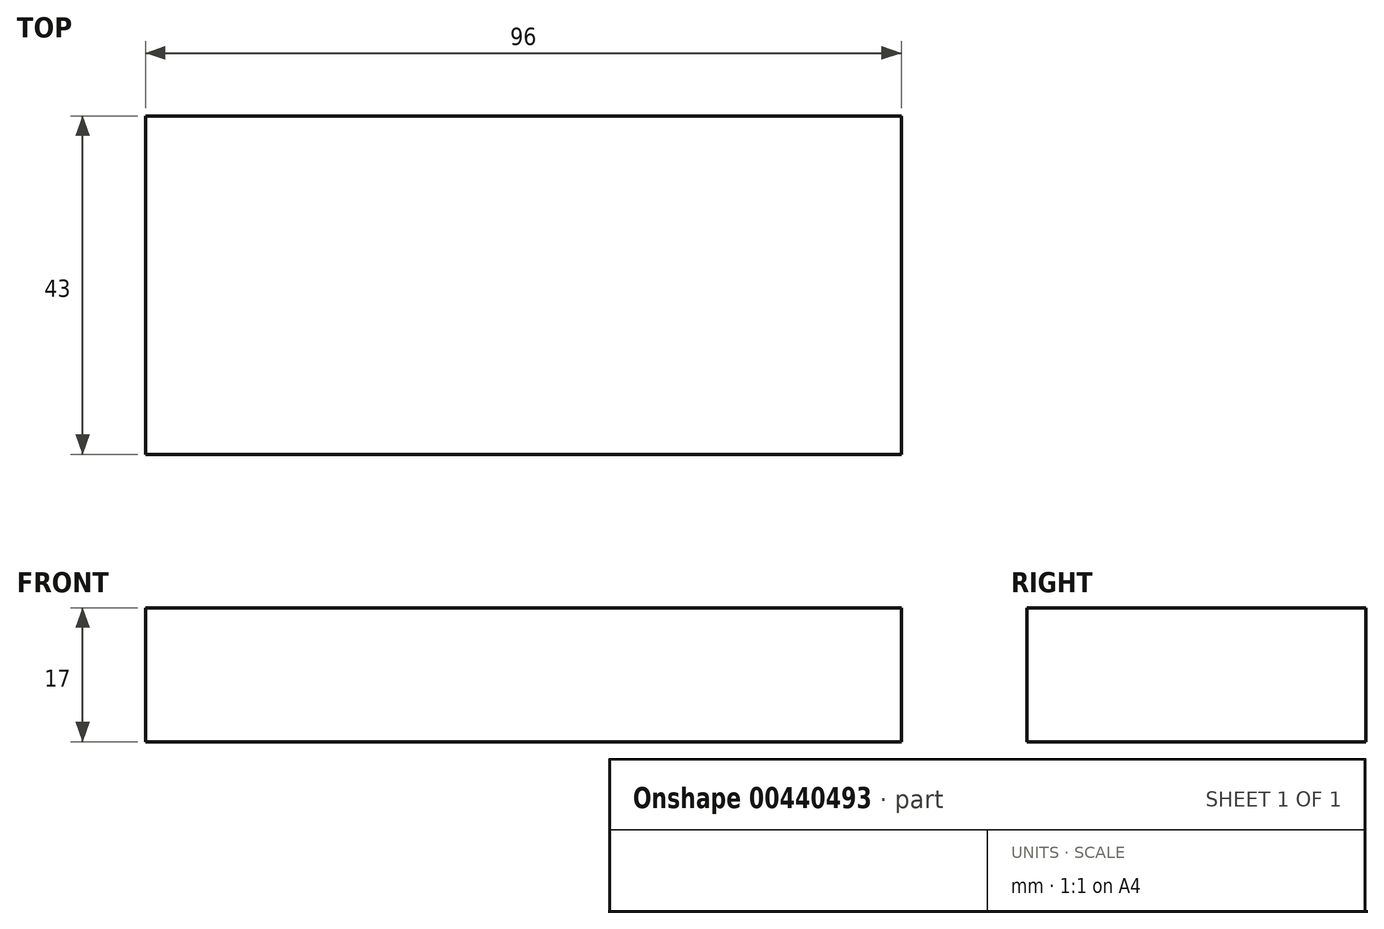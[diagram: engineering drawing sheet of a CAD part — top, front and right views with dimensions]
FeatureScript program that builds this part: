
annotation { "Feature Type Name" : "Feature", "Feature Type Description" : "" }
export const myFeature = defineFeature(function(context is Context, id is Id, definition is map)
    precondition{}
    {
        {
            var Q0;
            Q0=qCreatedBy(makeId("Top.planeOp"),FACE);
            var sketch = newSketch(context, id + "F0", { "sketchPlane" : qUnion([Q0])});
            skLineSegment(sketch, "E0.bottom", {"start": v(48, -21.5) * mm, "end": v(-48, -21.5) * mm});
            skLineSegment(sketch, "E0.top", {"start": v(48, 21.5) * mm, "end": v(-48, 21.5) * mm});
            skLineSegment(sketch, "E0.left", {"start": v(48, -21.5) * mm, "end": v(48, 21.5) * mm});
            skLineSegment(sketch, "E0.right", {"start": v(-48, -21.5) * mm, "end": v(-48, 21.5) * mm});
            skPoint(sketch, "E0.middle", {"position": v(0, 0) * mm});
            skSolve(sketch);
        }
        {
            var Q0;
            Q0 = qSketchRegion(id + "F0", true);
            extrude(context, id + "F1", {"entities" : qUnion([Q0]), "depth" : 17 * mm});
        }
    });
